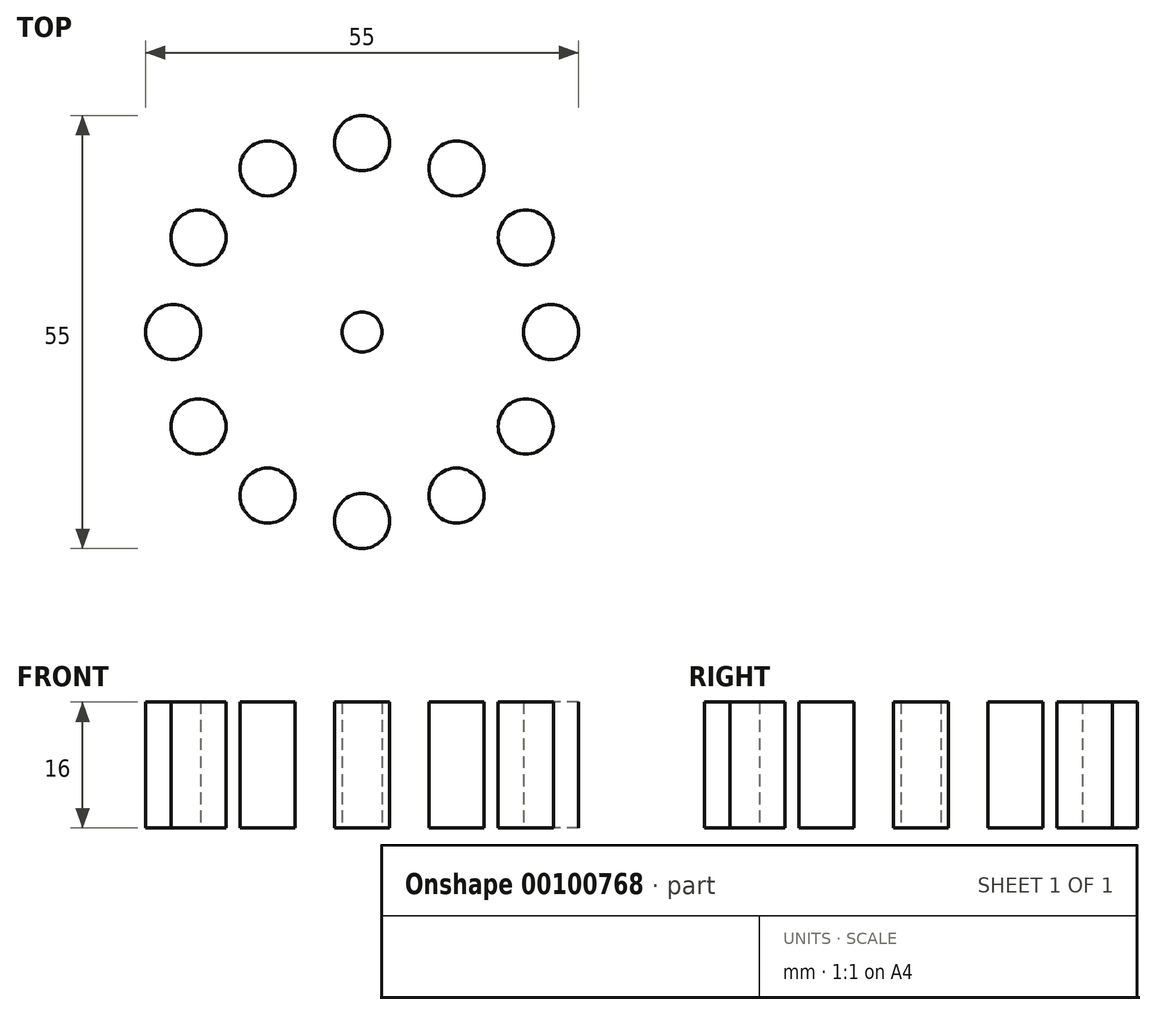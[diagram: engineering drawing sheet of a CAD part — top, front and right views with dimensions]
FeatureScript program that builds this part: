
annotation { "Feature Type Name" : "Feature", "Feature Type Description" : "" }
export const myFeature = defineFeature(function(context is Context, id is Id, definition is map)
    precondition{}
    {
        {
            var Q0;
            Q0=qCreatedBy(makeId("Top.planeOp"),FACE);
            var sketch = newSketch(context, id + "F0", { "sketchPlane" : qUnion([Q0])});
            skCircle(sketch, "E0", {"center": v(0, 0) * mm, "radius": 20.5 * mm, "construction": true});
            skCircle(sketch, "E1", {"center": v(0, 0) * mm, "radius": 27.5 * mm, "construction": true});
            skLineSegment(sketch, "E2", {"start": v(0, 27.5) * mm, "end": v(0, 20.5) * mm, "construction": true});
            skCircle(sketch, "E3", {"center": v(0, 24) * mm, "radius": 3.5 * mm});
            skCircle(sketch, "E4.1.0", {"center": v(-12, 20.78) * mm, "radius": 3.5 * mm});
            skCircle(sketch, "E4.2.0", {"center": v(-20.78, 12) * mm, "radius": 3.5 * mm});
            skCircle(sketch, "E4.3.0", {"center": v(-24, 0) * mm, "radius": 3.5 * mm});
            skCircle(sketch, "E4.4.0", {"center": v(-20.78, -12) * mm, "radius": 3.5 * mm});
            skCircle(sketch, "E4.5.0", {"center": v(-12, -20.78) * mm, "radius": 3.5 * mm});
            skCircle(sketch, "E4.6.0", {"center": v(0, -24) * mm, "radius": 3.5 * mm});
            skCircle(sketch, "E4.7.0", {"center": v(12, -20.78) * mm, "radius": 3.5 * mm});
            skCircle(sketch, "E4.8.0", {"center": v(20.78, -12) * mm, "radius": 3.5 * mm});
            skCircle(sketch, "E4.9.0", {"center": v(24, 0) * mm, "radius": 3.5 * mm});
            skCircle(sketch, "E4.10.0", {"center": v(20.78, 12) * mm, "radius": 3.5 * mm});
            skCircle(sketch, "E4.11.0", {"center": v(12, 20.78) * mm, "radius": 3.5 * mm});
            skLineSegment(sketch, "E5", {"start": v(24, 0) * mm, "end": v(0, 0) * mm, "construction": true});
            skLineSegment(sketch, "E6", {"start": v(0, 0) * mm, "end": v(20.78, 12) * mm, "construction": true});
            skLineSegment(sketch, "E7", {"start": v(20.78, 12) * mm, "end": v(24, 0) * mm, "construction": true});
            skCircle(sketch, "E8", {"center": v(0, 0) * mm, "radius": 2.55 * mm});
            skSolve(sketch);
        }
        {
            var Q0;
            Q0=makeQuery(id+"F0.imprint","IMPRINT",FACE,{"disambiguationData":[TD([[makeQuery(id+"F0.imprint","IMPRINT",EDGE,{"derivedFrom":sQuery(id+"F0.wireOp",EDGE,"E4.10.0")}),1.0]])]});
            var Q1;
            Q1=makeQuery(id+"F0.imprint","IMPRINT",FACE,{"disambiguationData":[TD([[makeQuery(id+"F0.imprint","IMPRINT",EDGE,{"derivedFrom":sQuery(id+"F0.wireOp",EDGE,"E4.9.0")}),1.0]])]});
            var Q2;
            Q2=makeQuery(id+"F0.imprint","IMPRINT",FACE,{"disambiguationData":[TD([[makeQuery(id+"F0.imprint","IMPRINT",EDGE,{"derivedFrom":sQuery(id+"F0.wireOp",EDGE,"E4.11.0")}),1.0]])]});
            var Q3;
            Q3=makeQuery(id+"F0.imprint","IMPRINT",FACE,{"disambiguationData":[TD([[makeQuery(id+"F0.imprint","IMPRINT",EDGE,{"derivedFrom":sQuery(id+"F0.wireOp",EDGE,"E4.8.0")}),1.0]])]});
            var Q4;
            Q4=makeQuery(id+"F0.imprint","IMPRINT",FACE,{"disambiguationData":[TD([[makeQuery(id+"F0.imprint","IMPRINT",EDGE,{"derivedFrom":sQuery(id+"F0.wireOp",EDGE,"E4.7.0")}),1.0]])]});
            var Q5;
            Q5=makeQuery(id+"F0.imprint","IMPRINT",FACE,{"disambiguationData":[TD([[makeQuery(id+"F0.imprint","IMPRINT",EDGE,{"derivedFrom":sQuery(id+"F0.wireOp",EDGE,"E4.6.0")}),1.0]])]});
            var Q6;
            Q6=makeQuery(id+"F0.imprint","IMPRINT",FACE,{"disambiguationData":[TD([[makeQuery(id+"F0.imprint","IMPRINT",EDGE,{"derivedFrom":sQuery(id+"F0.wireOp",EDGE,"E4.5.0")}),1.0]])]});
            var Q7;
            Q7=makeQuery(id+"F0.imprint","IMPRINT",FACE,{"disambiguationData":[TD([[makeQuery(id+"F0.imprint","IMPRINT",EDGE,{"derivedFrom":sQuery(id+"F0.wireOp",EDGE,"E4.4.0")}),1.0]])]});
            var Q8;
            Q8=makeQuery(id+"F0.imprint","IMPRINT",FACE,{"disambiguationData":[TD([[makeQuery(id+"F0.imprint","IMPRINT",EDGE,{"derivedFrom":sQuery(id+"F0.wireOp",EDGE,"E4.3.0")}),1.0]])]});
            var Q9;
            Q9=makeQuery(id+"F0.imprint","IMPRINT",FACE,{"disambiguationData":[TD([[makeQuery(id+"F0.imprint","IMPRINT",EDGE,{"derivedFrom":sQuery(id+"F0.wireOp",EDGE,"E4.2.0")}),1.0]])]});
            var Q10;
            Q10=makeQuery(id+"F0.imprint","IMPRINT",FACE,{"disambiguationData":[TD([[makeQuery(id+"F0.imprint","IMPRINT",EDGE,{"derivedFrom":sQuery(id+"F0.wireOp",EDGE,"E4.1.0")}),1.0]])]});
            var Q11;
            Q11=makeQuery(id+"F0.imprint","IMPRINT",FACE,{"disambiguationData":[TD([[makeQuery(id+"F0.imprint","IMPRINT",EDGE,{"derivedFrom":sQuery(id+"F0.wireOp",EDGE,"E3")}),1.0]])]});
            var Q12;
            Q12=makeQuery(id+"F0.imprint","IMPRINT",FACE,{"disambiguationData":[TD([[makeQuery(id+"F0.imprint","IMPRINT",EDGE,{"derivedFrom":sQuery(id+"F0.wireOp",EDGE,"E8")}),1.0]])]});
            extrude(context, id + "F1", {"entities" : qUnion([Q0, Q1, Q2, Q3, Q4, Q5, Q6, Q7, Q8, Q9, Q10, Q11, Q12]), "depth" : 16 * mm});
        }
    });
